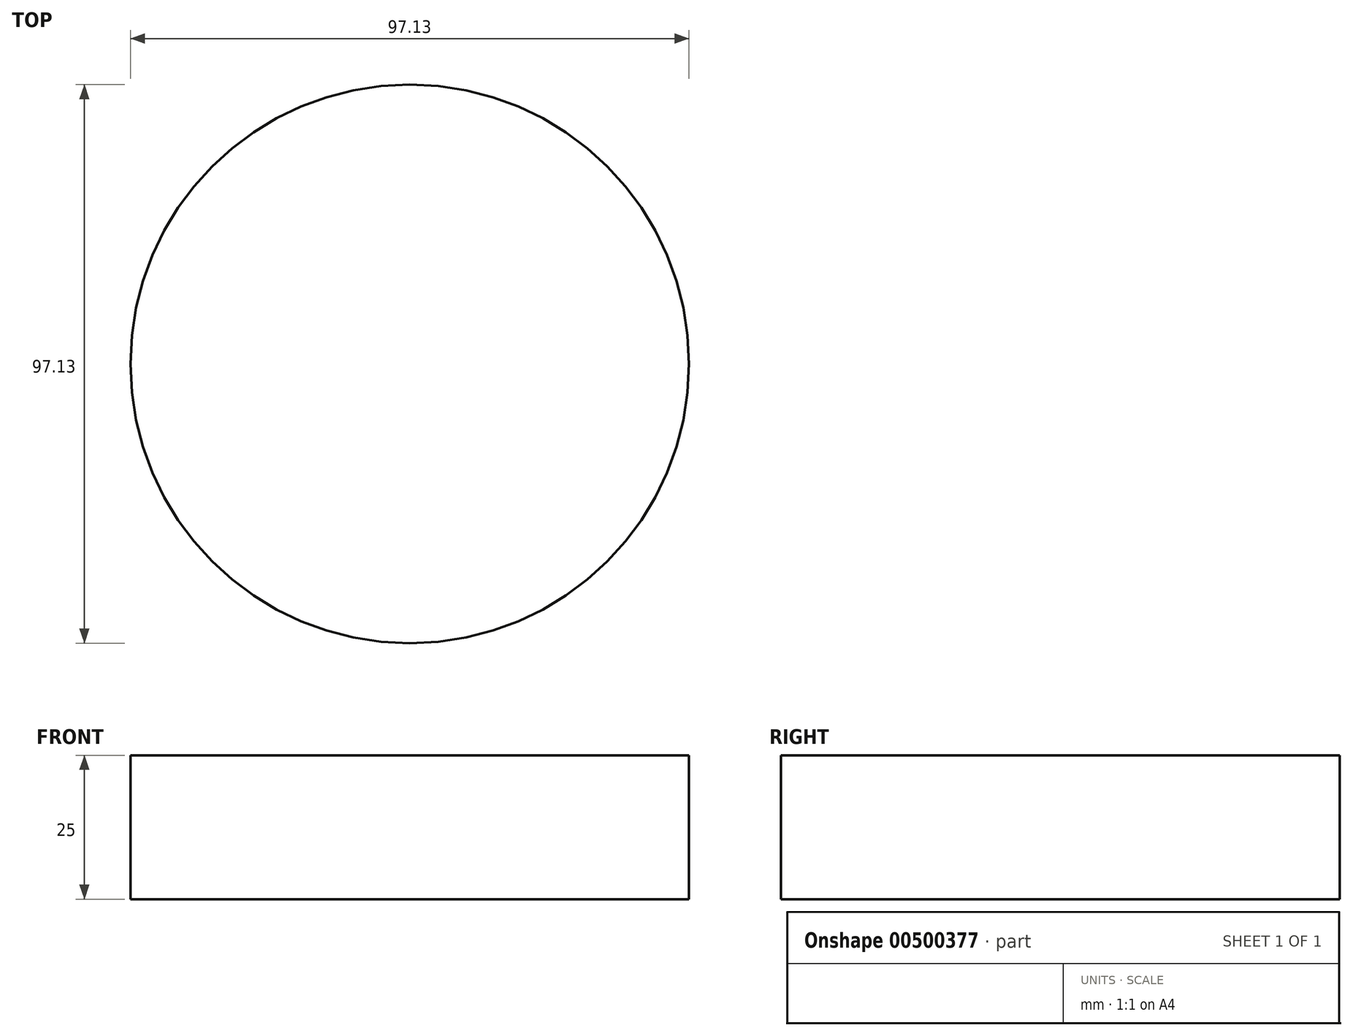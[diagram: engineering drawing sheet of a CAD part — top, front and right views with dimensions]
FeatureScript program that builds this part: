
annotation { "Feature Type Name" : "Feature", "Feature Type Description" : "" }
export const myFeature = defineFeature(function(context is Context, id is Id, definition is map)
    precondition{}
    {
        {
            var Q0;
            Q0=qCreatedBy(makeId("Top.planeOp"),FACE);
            var sketch = newSketch(context, id + "F0", { "sketchPlane" : qUnion([Q0])});
            skCircle(sketch, "E0", {"center": v(-49.25, 34.94) * mm, "radius": 48.57 * mm});
            skSolve(sketch);
        }
        {
            var Q0;
            Q0 = qSketchRegion(id + "F0", true);
            extrude(context, id + "F1", {"entities" : qUnion([Q0]), "depth" : 25 * mm});
        }
    });
